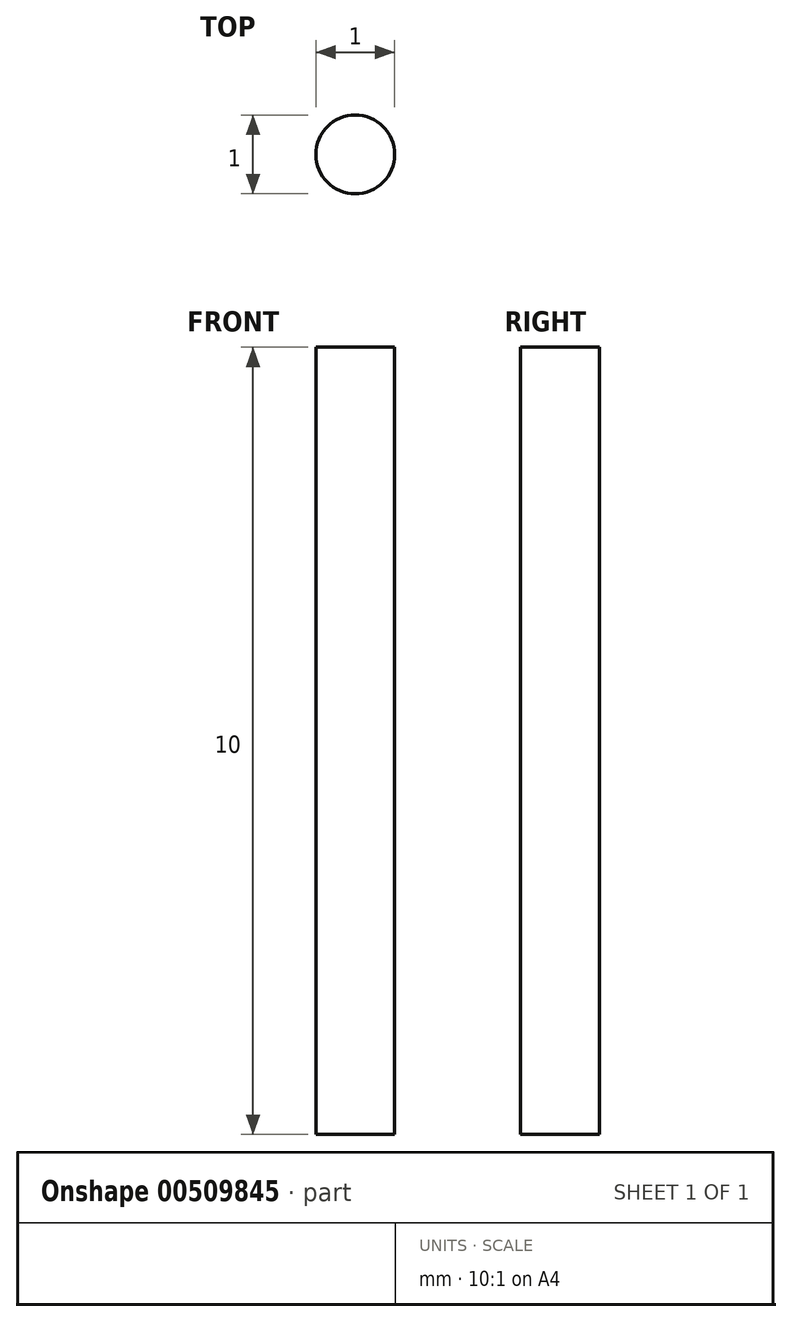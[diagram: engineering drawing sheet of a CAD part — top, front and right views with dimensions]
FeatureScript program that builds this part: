
annotation { "Feature Type Name" : "Feature", "Feature Type Description" : "" }
export const myFeature = defineFeature(function(context is Context, id is Id, definition is map)
    precondition{}
    {
        {
            var Q0;
            Q0=qCreatedBy(makeId("Top.planeOp"),FACE);
            var sketch = newSketch(context, id + "F0", { "sketchPlane" : qUnion([Q0])});
            skCircle(sketch, "E0", {"center": v(0, 0) * mm, "radius": 0.5 * mm});
            skSolve(sketch);
        }
        {
            var Q0;
            Q0 = qSketchRegion(id + "F0", true);
            extrude(context, id + "F1", {"entities" : qUnion([Q0]), "depth" : 10 * mm});
        }
    });
